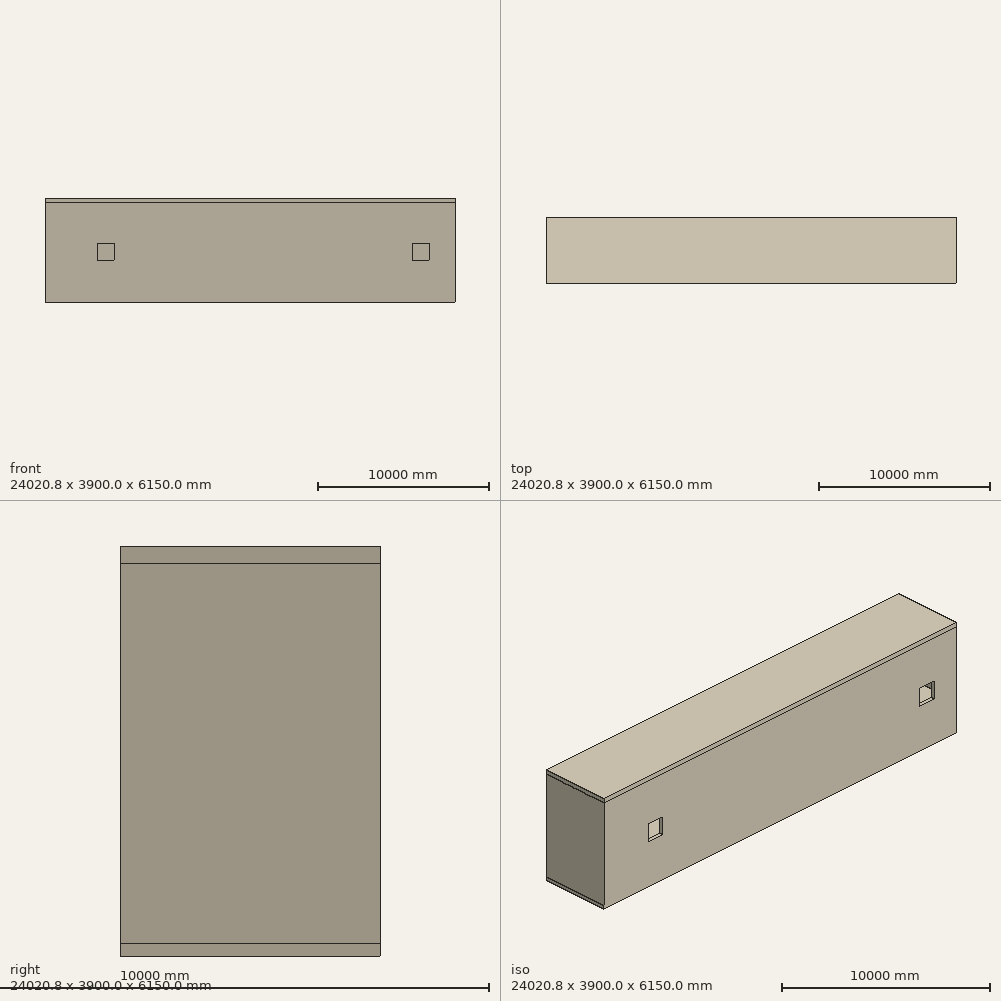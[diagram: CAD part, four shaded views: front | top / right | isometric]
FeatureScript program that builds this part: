
annotation { "Feature Type Name" : "Feature", "Feature Type Description" : "" }
export const myFeature = defineFeature(function(context is Context, id is Id, definition is map)
    precondition{}
    {
        {
            var Q0;
            Q0=qCreatedBy(makeId("Top.planeOp"),FACE);
            var sketch = newSketch(context, id + "F0", { "sketchPlane" : qUnion([Q0])});
            skLineSegment(sketch, "E0.bottom", {"start": v(0, 0) * mm, "end": v(4000, 0) * mm});
            skLineSegment(sketch, "E0.top", {"start": v(0, -3900) * mm, "end": v(4000, -3900) * mm});
            skLineSegment(sketch, "E0.left", {"start": v(0, -200) * mm, "end": v(0, -3700) * mm});
            skLineSegment(sketch, "E0.right", {"start": v(4000, 0) * mm, "end": v(4000, -3900) * mm});
            skLineSegment(sketch, "E1.0", {"start": v(200, -200) * mm, "end": v(3800, -200) * mm});
            skLineSegment(sketch, "E1.1", {"start": v(200, -200) * mm, "end": v(200, -3700) * mm});
            skLineSegment(sketch, "E1.2", {"start": v(200, -3700) * mm, "end": v(3800, -3700) * mm});
            skLineSegment(sketch, "E1.3", {"start": v(3800, -200) * mm, "end": v(3800, -3700) * mm});
            skLineSegment(sketch, "E2.bottom", {"start": v(0, 0) * mm, "end": v(-6000, 0) * mm});
            skLineSegment(sketch, "E2.top", {"start": v(0, -3900) * mm, "end": v(-6000, -3900) * mm});
            skLineSegment(sketch, "E2.right", {"start": v(-6000, -200) * mm, "end": v(-6000, -3700) * mm});
            skLineSegment(sketch, "E3.0", {"start": v(0, -3700) * mm, "end": v(-5800, -3700) * mm});
            skLineSegment(sketch, "E3.1", {"start": v(-5800, -200) * mm, "end": v(-5800, -3700) * mm});
            skLineSegment(sketch, "E3.2", {"start": v(0, -200) * mm, "end": v(-5800, -200) * mm});
            skLineSegment(sketch, "E4.bottom", {"start": v(-6000, 0) * mm, "end": v(-12000, 0) * mm});
            skLineSegment(sketch, "E4.top", {"start": v(-6000, -3900) * mm, "end": v(-12000, -3900) * mm});
            skLineSegment(sketch, "E4.right", {"start": v(-12000, -200) * mm, "end": v(-12000, -3700) * mm});
            skLineSegment(sketch, "E5.0", {"start": v(-6000, -3700) * mm, "end": v(-11800, -3700) * mm});
            skLineSegment(sketch, "E5.1", {"start": v(-11800, -200) * mm, "end": v(-11800, -3700) * mm});
            skLineSegment(sketch, "E5.2", {"start": v(-6000, -200) * mm, "end": v(-11800, -200) * mm});
            skLineSegment(sketch, "E6.bottom", {"start": v(-12000, 0) * mm, "end": v(-20000, 0) * mm});
            skLineSegment(sketch, "E6.top", {"start": v(-12000, -3900) * mm, "end": v(-20000, -3900) * mm});
            skLineSegment(sketch, "E6.right", {"start": v(-20000, 0) * mm, "end": v(-20000, -3900) * mm});
            skLineSegment(sketch, "E7.0", {"start": v(-12000, -3700) * mm, "end": v(-19800, -3700) * mm});
            skLineSegment(sketch, "E7.1", {"start": v(-19800, -200) * mm, "end": v(-19800, -3700) * mm});
            skLineSegment(sketch, "E7.2", {"start": v(-12000, -200) * mm, "end": v(-19800, -200) * mm});
            skSolve(sketch);
        }
        {
            var Q0;
            Q0 = qSketchRegion(id + "F0", true);
            extrude(context, id + "F1", {"entities" : qUnion([Q0]), "depth" : 4000 * mm});
        }
        {
            var Q0;
            Q0=makeQuery(id+"F1.opExtrude","CAP_FACE",FACE,{"disambiguationData":[OSD([sQuery(id+"F0.wireOp",EDGE,"E0.bottom"),sQuery(id+"F0.wireOp",EDGE,"E0.top"),sQuery(id+"F0.wireOp",EDGE,"E0.right"),sQuery(id+"F0.wireOp",EDGE,"E1.0"),sQuery(id+"F0.wireOp",EDGE,"E1.1"),sQuery(id+"F0.wireOp",EDGE,"E1.2"),sQuery(id+"F0.wireOp",EDGE,"E1.3"),sQuery(id+"F0.wireOp",EDGE,"E2.bottom"),sQuery(id+"F0.wireOp",EDGE,"E2.top"),sQuery(id+"F0.wireOp",EDGE,"E0.left"),sQuery(id+"F0.wireOp",EDGE,"E3.0"),sQuery(id+"F0.wireOp",EDGE,"E3.1"),sQuery(id+"F0.wireOp",EDGE,"E3.2"),sQuery(id+"F0.wireOp",EDGE,"E4.bottom"),sQuery(id+"F0.wireOp",EDGE,"E4.top"),sQuery(id+"F0.wireOp",EDGE,"E2.right"),sQuery(id+"F0.wireOp",EDGE,"E5.0"),sQuery(id+"F0.wireOp",EDGE,"E5.1"),sQuery(id+"F0.wireOp",EDGE,"E5.2"),sQuery(id+"F0.wireOp",EDGE,"E6.bottom"),sQuery(id+"F0.wireOp",EDGE,"E6.top"),sQuery(id+"F0.wireOp",EDGE,"E4.right"),sQuery(id+"F0.wireOp",EDGE,"E6.right"),sQuery(id+"F0.wireOp",EDGE,"E7.0"),sQuery(id+"F0.wireOp",EDGE,"E7.1"),sQuery(id+"F0.wireOp",EDGE,"E7.2")])],"isStart":true});
            var sketch = newSketch(context, id + "F2", { "sketchPlane" : qUnion([Q0])});
            skSolve(sketch);
        }
        {
            var Q0;
            Q0=makeQuery(id+"F2.imprint","IMPRINT",FACE,{"disambiguationData":[TD([[makeQuery(id+"F2.imprint","IMPRINT",EDGE,{"derivedFrom":makeQuery(id+"F1.opExtrude","CAP_EDGE",EDGE,{"disambiguationData":[OSD([sQuery(id+"F0.wireOp",EDGE,"E0.right")])],"isStart":true})}),1.0]])]});
            var sketch = newSketch(context, id + "F3", { "sketchPlane" : qUnion([Q0])});
            skLineSegment(sketch, "E8.bottom", {"start": v(4000, 0) * mm, "end": v(-20000, 0) * mm});
            skLineSegment(sketch, "E8.top", {"start": v(4000, 3900) * mm, "end": v(-20000, 3900) * mm});
            skLineSegment(sketch, "E8.left", {"start": v(4000, 0) * mm, "end": v(4000, 3900) * mm});
            skLineSegment(sketch, "E8.right", {"start": v(-20000, 0) * mm, "end": v(-20000, 3900) * mm});
            skSolve(sketch);
        }
        {
            var Q0;
            Q0 = qSketchRegion(id + "F3", true);
            extrude(context, id + "F4", {"entities" : qUnion([Q0]), "operationType" : NewBodyOperationType.ADD, "depth" : 200 * mm});
        }
        {
            var Q0;
            Q0=makeQuery(id+"F4.opExtrude","CAP_FACE",FACE,{"disambiguationData":[OSD([sQuery(id+"F3.wireOp",EDGE,"E8.bottom"),sQuery(id+"F3.wireOp",EDGE,"E8.top"),sQuery(id+"F3.wireOp",EDGE,"E8.left"),sQuery(id+"F3.wireOp",EDGE,"E8.right")])],"isStart":false});
            var sketch = newSketch(context, id + "F5", { "sketchPlane" : qUnion([Q0])});
            skLineSegment(sketch, "E9.bottom", {"start": v(4000, 0) * mm, "end": v(-20000, 0) * mm});
            skLineSegment(sketch, "E9.top", {"start": v(4000, 3900) * mm, "end": v(-20000, 3900) * mm});
            skLineSegment(sketch, "E9.left", {"start": v(4000, 0) * mm, "end": v(4000, 3900) * mm});
            skLineSegment(sketch, "E9.right", {"start": v(-20000, 0) * mm, "end": v(-20000, 3900) * mm});
            skLineSegment(sketch, "E10.0", {"start": v(3800, 200) * mm, "end": v(-19800, 200) * mm});
            skLineSegment(sketch, "E10.1", {"start": v(3800, 200) * mm, "end": v(3800, 3700) * mm});
            skLineSegment(sketch, "E10.2", {"start": v(3800, 3700) * mm, "end": v(-19800, 3700) * mm});
            skLineSegment(sketch, "E10.3", {"start": v(-19800, 200) * mm, "end": v(-19800, 3700) * mm});
            skSolve(sketch);
        }
        {
            var Q0;
            Q0 = qSketchRegion(id + "F5", true);
            extrude(context, id + "F6", {"entities" : qUnion([Q0]), "operationType" : NewBodyOperationType.ADD, "depth" : 1500 * mm});
        }
        {
            var Q0;
            Q0=makeQuery(id+"F6.opExtrude","CAP_FACE",FACE,{"disambiguationData":[OSD([sQuery(id+"F5.wireOp",EDGE,"E9.bottom"),sQuery(id+"F5.wireOp",EDGE,"E9.top"),sQuery(id+"F5.wireOp",EDGE,"E9.left"),sQuery(id+"F5.wireOp",EDGE,"E9.right"),sQuery(id+"F5.wireOp",EDGE,"E10.0"),sQuery(id+"F5.wireOp",EDGE,"E10.1"),sQuery(id+"F5.wireOp",EDGE,"E10.2"),sQuery(id+"F5.wireOp",EDGE,"E10.3")])],"isStart":false});
            var sketch = newSketch(context, id + "F7", { "sketchPlane" : qUnion([Q0])});
            skSolve(sketch);
        }
        {
            var Q0;
            Q0=makeQuery(id+"F7.imprint","IMPRINT",FACE,{"disambiguationData":[TD([[makeQuery(id+"F7.imprint","IMPRINT",EDGE,{"derivedFrom":makeQuery(id+"F6.opExtrude","CAP_EDGE",EDGE,{"disambiguationData":[OSD([sQuery(id+"F5.wireOp",EDGE,"E9.bottom")])],"isStart":false})}),1.0]])]});
            var sketch = newSketch(context, id + "F8", { "sketchPlane" : qUnion([Q0])});
            skLineSegment(sketch, "E11.bottom", {"start": v(3979.17, 3900) * mm, "end": v(-20020.83, 3900) * mm});
            skLineSegment(sketch, "E11.top", {"start": v(3979.17, 0) * mm, "end": v(-20020.83, 0) * mm});
            skLineSegment(sketch, "E11.left", {"start": v(3979.17, 3900) * mm, "end": v(3979.17, 0) * mm});
            skLineSegment(sketch, "E11.right", {"start": v(-20020.83, 3900) * mm, "end": v(-20020.83, 0) * mm});
            skSolve(sketch);
        }
        {
            var Q0;
            Q0 = qSketchRegion(id + "F8", true);
            extrude(context, id + "F9", {"entities" : qUnion([Q0]), "operationType" : NewBodyOperationType.ADD, "depth" : 200 * mm});
        }
        {
            var Q0;
            Q0=makeQuery(id+"F9.boolean.opBoolean","MERGE",FACE,{"derivedFrom":[makeQuery(id+"F6.boolean.opBoolean","MERGE",FACE,{"derivedFrom":[makeQuery(id+"F4.boolean.opBoolean","MERGE",FACE,{"derivedFrom":[makeQuery(id+"F1.opExtrude","SWEPT_FACE",FACE,{"disambiguationData":[OSD([sQuery(id+"F0.wireOp",EDGE,"E0.top"),sQuery(id+"F0.wireOp",EDGE,"E2.top"),sQuery(id+"F0.wireOp",EDGE,"E4.top"),sQuery(id+"F0.wireOp",EDGE,"E6.top")])]}),makeQuery(id+"F4.opExtrude","SWEPT_FACE",FACE,{"disambiguationData":[OSD([sQuery(id+"F3.wireOp",EDGE,"E8.top")])]})]}),makeQuery(id+"F6.opExtrude","SWEPT_FACE",FACE,{"disambiguationData":[OSD([sQuery(id+"F5.wireOp",EDGE,"E9.top")])]})]}),makeQuery(id+"F9.opExtrude","SWEPT_FACE",FACE,{"disambiguationData":[OSD([sQuery(id+"F8.wireOp",EDGE,"E11.bottom")])]})]});
            var sketch = newSketch(context, id + "F10", { "sketchPlane" : qUnion([Q0])});
            skLineSegment(sketch, "E12.bottom", {"start": v(1500, 1600) * mm, "end": v(2500, 1600) * mm});
            skLineSegment(sketch, "E12.top", {"start": v(1500, 600) * mm, "end": v(2500, 600) * mm});
            skLineSegment(sketch, "E12.left", {"start": v(1500, 1600) * mm, "end": v(1500, 600) * mm});
            skLineSegment(sketch, "E12.right", {"start": v(2500, 1600) * mm, "end": v(2500, 600) * mm});
            skSolve(sketch);
        }
        {
            var Q0;
            Q0 = qSketchRegion(id + "F10", true);
            extrude(context, id + "F11", {"entities" : qUnion([Q0]), "operationType" : NewBodyOperationType.REMOVE, "oppositeDirection" : true, "depth" : 250 * mm});
        }
        {
            var Q0;
            Q0=makeQuery(id+"F1.opExtrude","CAP_FACE",FACE,{"disambiguationData":[OSD([sQuery(id+"F0.wireOp",EDGE,"E0.bottom"),sQuery(id+"F0.wireOp",EDGE,"E0.top"),sQuery(id+"F0.wireOp",EDGE,"E0.right"),sQuery(id+"F0.wireOp",EDGE,"E1.0"),sQuery(id+"F0.wireOp",EDGE,"E1.1"),sQuery(id+"F0.wireOp",EDGE,"E1.2"),sQuery(id+"F0.wireOp",EDGE,"E1.3"),sQuery(id+"F0.wireOp",EDGE,"E2.bottom"),sQuery(id+"F0.wireOp",EDGE,"E2.top"),sQuery(id+"F0.wireOp",EDGE,"E0.left"),sQuery(id+"F0.wireOp",EDGE,"E3.0"),sQuery(id+"F0.wireOp",EDGE,"E3.1"),sQuery(id+"F0.wireOp",EDGE,"E3.2"),sQuery(id+"F0.wireOp",EDGE,"E4.bottom"),sQuery(id+"F0.wireOp",EDGE,"E4.top"),sQuery(id+"F0.wireOp",EDGE,"E2.right"),sQuery(id+"F0.wireOp",EDGE,"E5.0"),sQuery(id+"F0.wireOp",EDGE,"E5.1"),sQuery(id+"F0.wireOp",EDGE,"E5.2"),sQuery(id+"F0.wireOp",EDGE,"E6.bottom"),sQuery(id+"F0.wireOp",EDGE,"E6.top"),sQuery(id+"F0.wireOp",EDGE,"E4.right"),sQuery(id+"F0.wireOp",EDGE,"E6.right"),sQuery(id+"F0.wireOp",EDGE,"E7.0"),sQuery(id+"F0.wireOp",EDGE,"E7.1"),sQuery(id+"F0.wireOp",EDGE,"E7.2")])],"isStart":false});
            var sketch = newSketch(context, id + "F12", { "sketchPlane" : qUnion([Q0])});
            skLineSegment(sketch, "E13.bottom", {"start": v(-20000, 0) * mm, "end": v(4000, 0) * mm});
            skLineSegment(sketch, "E13.top", {"start": v(-20000, -3900) * mm, "end": v(4000, -3900) * mm});
            skLineSegment(sketch, "E13.left", {"start": v(-20000, 0) * mm, "end": v(-20000, -3900) * mm});
            skLineSegment(sketch, "E13.right", {"start": v(4000, 0) * mm, "end": v(4000, -3900) * mm});
            skSolve(sketch);
        }
        {
            var Q0;
            Q0 = qSketchRegion(id + "F12", true);
            extrude(context, id + "F13", {"entities" : qUnion([Q0]), "depth" : 250 * mm});
        }
        {
            var Q0;
            Q0=makeQuery(id+"F1.opExtrude","SWEPT_FACE",FACE,{"disambiguationData":[OSD([sQuery(id+"F0.wireOp",EDGE,"E1.1")])]});
            var sketch = newSketch(context, id + "F14", { "sketchPlane" : qUnion([Q0])});
            skLineSegment(sketch, "E14.bottom", {"start": v(-3650, 3800) * mm, "end": v(-250, 3800) * mm});
            skLineSegment(sketch, "E14.top", {"start": v(-3650, 2800) * mm, "end": v(-250, 2800) * mm});
            skLineSegment(sketch, "E14.left", {"start": v(-3650, 3800) * mm, "end": v(-3650, 2800) * mm});
            skLineSegment(sketch, "E14.right", {"start": v(-250, 3800) * mm, "end": v(-250, 2800) * mm});
            skSolve(sketch);
        }
        {
            var Q0;
            Q0 = qSketchRegion(id + "F14", true);
            extrude(context, id + "F15", {"entities" : qUnion([Q0]), "operationType" : NewBodyOperationType.REMOVE, "oppositeDirection" : true, "depth" : 250 * mm});
        }
        {
            var Q0;
            Q0=makeQuery(id+"F1.opExtrude","SWEPT_FACE",FACE,{"disambiguationData":[OSD([sQuery(id+"F0.wireOp",EDGE,"E3.1")])]});
            var sketch = newSketch(context, id + "F16", { "sketchPlane" : qUnion([Q0])});
            skLineSegment(sketch, "E15.bottom", {"start": v(-3650, 3750) * mm, "end": v(-250, 3750) * mm});
            skLineSegment(sketch, "E15.top", {"start": v(-3650, 2750) * mm, "end": v(-250, 2750) * mm});
            skLineSegment(sketch, "E15.left", {"start": v(-3650, 3750) * mm, "end": v(-3650, 2750) * mm});
            skLineSegment(sketch, "E15.right", {"start": v(-250, 3750) * mm, "end": v(-250, 2750) * mm});
            skSolve(sketch);
        }
        {
            var Q0;
            Q0 = qSketchRegion(id + "F16", true);
            extrude(context, id + "F17", {"entities" : qUnion([Q0]), "operationType" : NewBodyOperationType.REMOVE, "oppositeDirection" : true, "depth" : 250 * mm});
        }
        {
            var Q0;
            Q0=makeQuery(id+"F1.opExtrude","SWEPT_FACE",FACE,{"disambiguationData":[OSD([sQuery(id+"F0.wireOp",EDGE,"E5.1")])]});
            var sketch = newSketch(context, id + "F18", { "sketchPlane" : qUnion([Q0])});
            skLineSegment(sketch, "E16.bottom", {"start": v(-3650, 3750) * mm, "end": v(-250, 3750) * mm});
            skLineSegment(sketch, "E16.top", {"start": v(-3650, 2750) * mm, "end": v(-250, 2750) * mm});
            skLineSegment(sketch, "E16.left", {"start": v(-3650, 3750) * mm, "end": v(-3650, 2750) * mm});
            skLineSegment(sketch, "E16.right", {"start": v(-250, 3750) * mm, "end": v(-250, 2750) * mm});
            skSolve(sketch);
        }
        {
            var Q0;
            Q0 = qSketchRegion(id + "F18", true);
            extrude(context, id + "F19", {"entities" : qUnion([Q0]), "operationType" : NewBodyOperationType.REMOVE, "oppositeDirection" : true, "depth" : 250 * mm});
        }
        {
            var Q0;
            Q0=makeQuery(id+"F9.boolean.opBoolean","MERGE",FACE,{"derivedFrom":[makeQuery(id+"F6.boolean.opBoolean","MERGE",FACE,{"derivedFrom":[makeQuery(id+"F4.boolean.opBoolean","MERGE",FACE,{"derivedFrom":[makeQuery(id+"F1.opExtrude","SWEPT_FACE",FACE,{"disambiguationData":[OSD([sQuery(id+"F0.wireOp",EDGE,"E0.top"),sQuery(id+"F0.wireOp",EDGE,"E2.top"),sQuery(id+"F0.wireOp",EDGE,"E4.top"),sQuery(id+"F0.wireOp",EDGE,"E6.top")])]}),makeQuery(id+"F4.opExtrude","SWEPT_FACE",FACE,{"disambiguationData":[OSD([sQuery(id+"F3.wireOp",EDGE,"E8.top")])]})]}),makeQuery(id+"F6.opExtrude","SWEPT_FACE",FACE,{"disambiguationData":[OSD([sQuery(id+"F5.wireOp",EDGE,"E9.top")])]})]}),makeQuery(id+"F9.opExtrude","SWEPT_FACE",FACE,{"disambiguationData":[OSD([sQuery(id+"F8.wireOp",EDGE,"E11.bottom")])]})]});
            var sketch = newSketch(context, id + "F20", { "sketchPlane" : qUnion([Q0])});
            skLineSegment(sketch, "E17.bottom", {"start": v(-17000, 1600) * mm, "end": v(-16000, 1600) * mm});
            skLineSegment(sketch, "E17.top", {"start": v(-17000, 600) * mm, "end": v(-16000, 600) * mm});
            skLineSegment(sketch, "E17.left", {"start": v(-17000, 1600) * mm, "end": v(-17000, 600) * mm});
            skLineSegment(sketch, "E17.right", {"start": v(-16000, 1600) * mm, "end": v(-16000, 600) * mm});
            skSolve(sketch);
        }
        {
            var Q0;
            Q0 = qSketchRegion(id + "F20", true);
            extrude(context, id + "F21", {"entities" : qUnion([Q0]), "operationType" : NewBodyOperationType.REMOVE, "oppositeDirection" : true, "depth" : 250 * mm});
        }
        {
            var Q0;
            Q0=makeQuery(id+"F9.boolean.opBoolean","MERGE",FACE,{"derivedFrom":[makeQuery(id+"F6.boolean.opBoolean","MERGE",FACE,{"derivedFrom":[makeQuery(id+"F4.boolean.opBoolean","MERGE",FACE,{"derivedFrom":[makeQuery(id+"F1.opExtrude","SWEPT_FACE",FACE,{"disambiguationData":[OSD([sQuery(id+"F0.wireOp",EDGE,"E0.bottom"),sQuery(id+"F0.wireOp",EDGE,"E2.bottom"),sQuery(id+"F0.wireOp",EDGE,"E4.bottom"),sQuery(id+"F0.wireOp",EDGE,"E6.bottom")])]}),makeQuery(id+"F4.opExtrude","SWEPT_FACE",FACE,{"disambiguationData":[OSD([sQuery(id+"F3.wireOp",EDGE,"E8.bottom")])]})]}),makeQuery(id+"F6.opExtrude","SWEPT_FACE",FACE,{"disambiguationData":[OSD([sQuery(id+"F5.wireOp",EDGE,"E9.bottom")])]})]}),makeQuery(id+"F9.opExtrude","SWEPT_FACE",FACE,{"disambiguationData":[OSD([sQuery(id+"F8.wireOp",EDGE,"E11.top")])]})]});
            var sketch = newSketch(context, id + "F22", { "sketchPlane" : qUnion([Q0])});
            skLineSegment(sketch, "E18.bottom", {"start": v(6500, 750) * mm, "end": v(11500, 750) * mm});
            skLineSegment(sketch, "E18.top", {"start": v(6500, 0) * mm, "end": v(11500, 0) * mm});
            skLineSegment(sketch, "E18.left", {"start": v(6500, 750) * mm, "end": v(6500, 0) * mm});
            skLineSegment(sketch, "E18.right", {"start": v(11500, 750) * mm, "end": v(11500, 0) * mm});
            skSolve(sketch);
        }
        {
            var Q0;
            Q0 = qSketchRegion(id + "F22", true);
            extrude(context, id + "F23", {"entities" : qUnion([Q0]), "operationType" : NewBodyOperationType.REMOVE, "oppositeDirection" : true, "depth" : 250 * mm});
        }
    });
